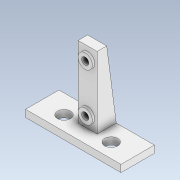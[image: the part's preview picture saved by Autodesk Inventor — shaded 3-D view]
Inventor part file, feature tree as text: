
AUTODESK INVENTOR PART (.ipt)
format: ipt  version: 2022 (Build 260153000, 153)  size: 205,824 bytes
history: native  units: mm
features: sketch x11, extrude x10, projected_geometry x4
ambient origin geometry x8: Origin, YZ Plane, XZ Plane, XY Plane, X Axis, Y Axis, Z Axis, Center Point
bodies: Solid1 (feature_tree)
feature tree (25):
  extrude  "Extrusion1"  Depth=50.0mm
  extrude  "Extrusion6"  Depth=5.5mm
  extrude  "Extrusion8"  Depth=3.0mm
  extrude  "Extrusion9"  Depth=4.0mm
  extrude  "Extrusion10"  Depth=30.0mm TaperAngle=0.0deg
  extrude  "Extrusion7"  Depth=1.0mm
  extrude  "Extrusion11"  Depth=10.0mm
  extrude  "Extrusion12"  Depth=3.0mm
  sketch  "Sketch13"  dims[d34=3.0mm d35=30.0mm d36=0.0mm]
  sketch  "Sketch14"  dims[d37=5.0mm d38=0.0mm d39=5.0mm d40=0.0mm]
  extrude  "Extrusion14"  Depth=30.0mm TaperAngle=0.0deg
  extrude  "Extrusion15"  Depth=5.0mm TaperAngle=0.0deg
  sketch  "Sketch1"  dims[d0=25.0mm d1=50.0mm]
  sketch  "Sketch6"  dims[d2=5.5mm d3=5.5mm]
  sketch  "Sketch7"  dims[d4=3.0mm d5=0.0mm d22=3.0mm]
  sketch  "Sketch8"  dims[d23=4.0mm d24=4.0mm]
  projected_geometry  "Projected Loop3"
  sketch  "Sketch9"  dims[d25=6.0mm d26=30.0mm d27=0.0mm]
  projected_geometry  "Projected Loop4"
  sketch  "Sketch10"  dims[d28=1.0mm d29=1.0mm]
  sketch  "Sketch11"  dims[d30=10.0mm d31=20.0mm]
  sketch  "Sketch12"  dims[d32=4.0mm d33=3.0mm]
  projected_geometry  "Projected Loop5"
  projected_geometry  "Projected Loop6"
  sketch  "Sketch15"  dims[d41=4.0mm d42=8.0mm d43=0.0mm d44=6.0mm d45=6.0mm d46=1.0mm d47=0.0mm d48=2.0mm d49=0.0mm d52=10.0mm d53=0.0mm d54=2.0mm d55=0.0mm d56=0.0mm]
